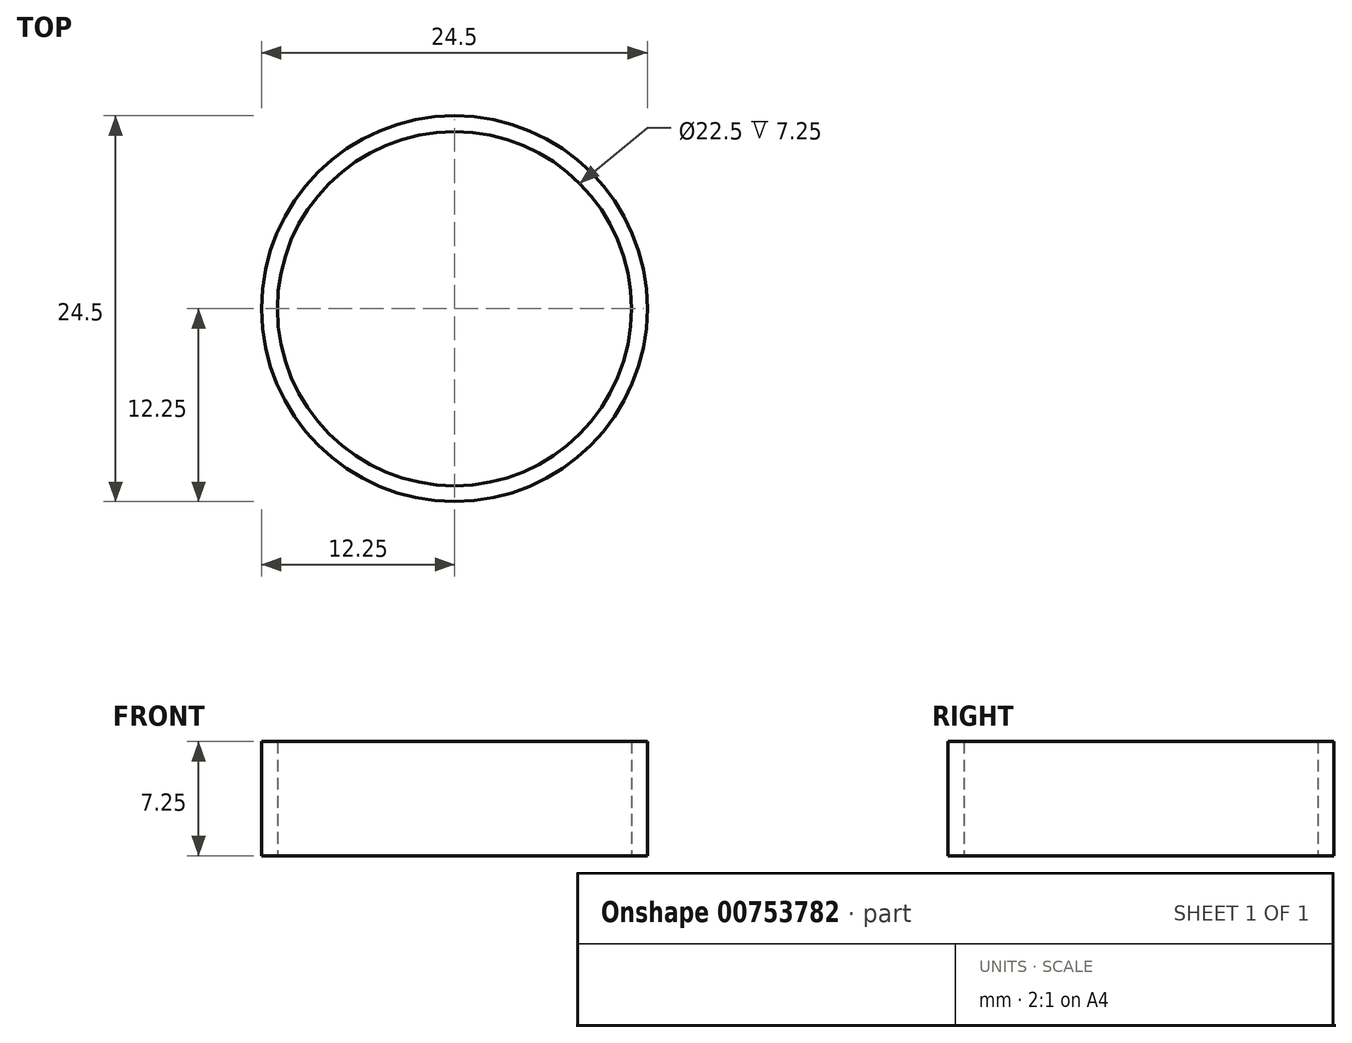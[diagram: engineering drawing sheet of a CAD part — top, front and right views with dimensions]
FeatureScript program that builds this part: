
annotation { "Feature Type Name" : "Feature", "Feature Type Description" : "" }
export const myFeature = defineFeature(function(context is Context, id is Id, definition is map)
    precondition{}
    {
        {
            var Q0;
            Q0=qCreatedBy(makeId("Top.planeOp"),FACE);
            var sketch = newSketch(context, id + "F0", { "sketchPlane" : qUnion([Q0])});
            skCircle(sketch, "E0", {"center": v(0, 0) * mm, "radius": 11.25 * mm});
            skCircle(sketch, "E1", {"center": v(0, 0) * mm, "radius": 12.25 * mm});
            skSolve(sketch);
        }
        {
            var Q0;
            Q0 = qSketchRegion(id + "F0", true);
            extrude(context, id + "F1", {"entities" : qUnion([Q0]), "depth" : 7.25 * mm, "offsetDistance" : 25 * mm});
        }
    });
